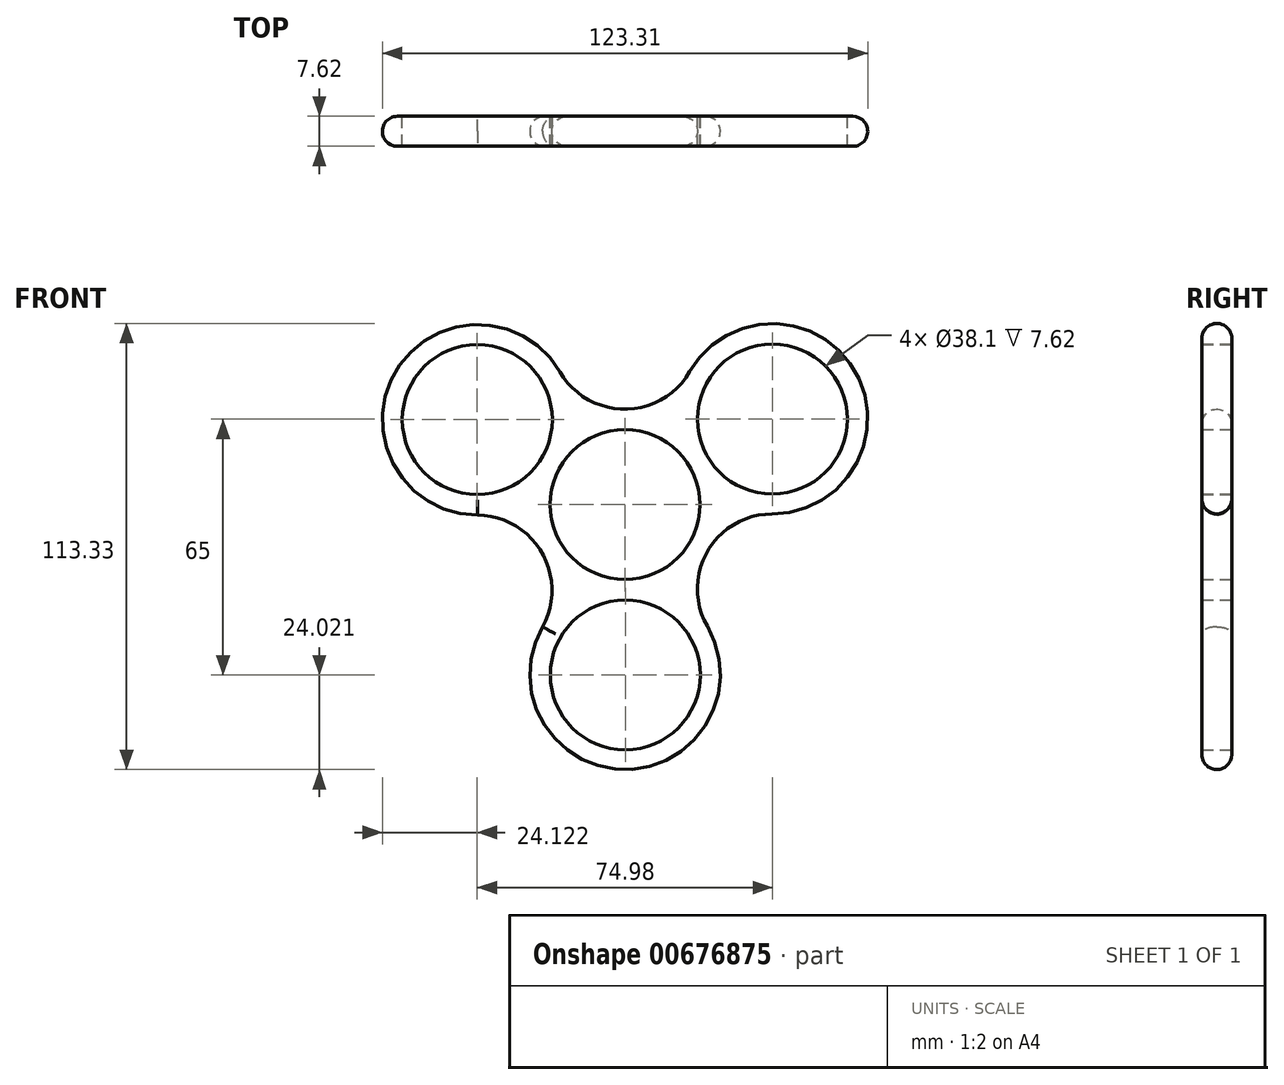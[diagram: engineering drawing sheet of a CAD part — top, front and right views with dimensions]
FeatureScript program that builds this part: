
annotation { "Feature Type Name" : "Feature", "Feature Type Description" : "" }
export const myFeature = defineFeature(function(context is Context, id is Id, definition is map)
    precondition{}
    {
        {
            var Q0;
            Q0=qCreatedBy(makeId("Front.planeOp"),FACE);
            var sketch = newSketch(context, id + "F0", { "sketchPlane" : qUnion([Q0])});
            skPoint(sketch, "E0.0.midPoint", {"position": v(18.8, -32.43) * mm});
            skCircle(sketch, "E1", {"center": v(0, 0) * mm, "radius": 19.05 * mm});
            skCircle(sketch, "E2", {"center": v(-37.53, 21.58) * mm, "radius": 19.05 * mm});
            skCircle(sketch, "E3", {"center": v(37.45, 21.71) * mm, "radius": 19.05 * mm});
            skCircle(sketch, "E4", {"center": v(0.08, -43.29) * mm, "radius": 19.05 * mm});
            skArc(sketch, "E5", {"start": v(-16.56, 33.74) * mm, "mid": v(-0.04, 24.24) * mm, "end": v(16.44, 33.8) * mm});
            skArc(sketch, "E6", {"start": v(37.4, -2.38) * mm, "mid": v(20.95, -11.9) * mm, "end": v(20.91, -30.9) * mm});
            skArc(sketch, "E7", {"start": v(-20.96, -31.05) * mm, "mid": v(-21.17, -12.17) * mm, "end": v(-37.49, -2.66) * mm});
            skArc(sketch, "E8", {"start": v(-16.56, 33.74) * mm, "mid": v(-58.43, 33.6) * mm, "end": v(-37.49, -2.66) * mm});
            skArc(sketch, "E9", {"start": v(37.4, -2.38) * mm, "mid": v(58.4, 33.96) * mm, "end": v(16.44, 33.8) * mm});
            skArc(sketch, "E10", {"start": v(-20.96, -31.05) * mm, "mid": v(0.1, -67.3) * mm, "end": v(20.91, -30.9) * mm});
            skSolve(sketch);
        }
        {
            var Q0;
            Q0=makeQuery(id+"F0.imprint","IMPRINT",FACE,{"disambiguationData":[TD([[makeQuery(id+"F0.imprint","IMPRINT",EDGE,{"derivedFrom":sQuery(id+"F0.wireOp",EDGE,"E1")}),-1.0]])]});
            extrude(context, id + "F1", {"entities" : qUnion([Q0]), "depth" : 7.62 * mm, "offsetDistance" : 25.4 * mm});
        }
        {
            var Q0;
            Q0=makeQuery(id+"F1.opExtrude","CAP_EDGE",EDGE,{"disambiguationData":[OSD([sQuery(id+"F0.wireOp",EDGE,"E5")])],"isStart":false});
            var Q1;
            Q1=makeQuery(id+"F1.opExtrude","CAP_EDGE",EDGE,{"disambiguationData":[OSD([sQuery(id+"F0.wireOp",EDGE,"E9")])],"isStart":false});
            var Q2;
            Q2=makeQuery(id+"F1.opExtrude","CAP_EDGE",EDGE,{"disambiguationData":[OSD([sQuery(id+"F0.wireOp",EDGE,"E10")])],"isStart":false});
            var Q3;
            Q3=makeQuery(id+"F1.opExtrude","CAP_EDGE",EDGE,{"disambiguationData":[OSD([sQuery(id+"F0.wireOp",EDGE,"E7")])],"isStart":false});
            var Q4;
            Q4=makeQuery(id+"F1.opExtrude","CAP_EDGE",EDGE,{"disambiguationData":[OSD([sQuery(id+"F0.wireOp",EDGE,"E8")])],"isStart":false});
            var Q5;
            Q5=makeQuery(id+"F1.opExtrude","CAP_EDGE",EDGE,{"disambiguationData":[OSD([sQuery(id+"F0.wireOp",EDGE,"E6")])],"isStart":true});
            var Q6;
            Q6=makeQuery(id+"F1.opExtrude","CAP_EDGE",EDGE,{"disambiguationData":[OSD([sQuery(id+"F0.wireOp",EDGE,"E10")])],"isStart":true});
            var Q7;
            Q7=makeQuery(id+"F1.opExtrude","CAP_EDGE",EDGE,{"disambiguationData":[OSD([sQuery(id+"F0.wireOp",EDGE,"E9")])],"isStart":true});
            var Q8;
            Q8=makeQuery(id+"F1.opExtrude","CAP_EDGE",EDGE,{"disambiguationData":[OSD([sQuery(id+"F0.wireOp",EDGE,"E8")])],"isStart":true});
            fillet(context, id + "F2", {"entities" : qUnion([Q0, Q1, Q2, Q3, Q4, Q5, Q6, Q7, Q8]), "radius" : 3.8 * mm, "tangentPropagation" : true, "allowEdgeOverflow" : false});
        }
    });
